# Revit family: Storage-Teknion-PLCS_Combo_Cabinet_Standard-R2015
name_source: partatom
category: Furniture
revit_build: Autodesk Revit Architecture 2015 (Build: 20140323_1530(x64)
units: mm (PartAtom-declared; Revit-internal decimal feet)

## types (3) — shared parameters
Assembly Code = E2020200
Lock Finish = Stainless Steel, Polished
Manufacturer = Teknion
Manufacturer Fax = 416.661.4586
Part Number = PLCS
Product Documentation Link = http://www.teknion.com
Product Line = Filing and Storage
Product Page URL = http://www.teknion.com
Series = Ledger Plus
Sustainability Data = http://www.teknion.com
URL = www.teknion.com
Unit Weight URL = http://www.teknion.com
Warranty = http://www.teknion.com

## per-type parameters (varying)
| type | Description | Four High Configuration | Height | Model | Three High Configuration |
| Freestanding Three - High | Combo Cabinets - Standard Freestanding Three High | No | 40 " | PLCSF3_ | Yes |
| Worksurface and Storage Supporting Three - High | Combo Cabinets - Standard Supporting Three High | No | 40 " | PLCSW4_ | Yes |
| Freestanding Four - High | Combo Cabinets - Standard Freestanding Four High | Yes | 48 " | PLCSF4_ | No |

## geometry (parser evidence)
native form markers: Sweep x2
no freeform markers — native parametric forms only
